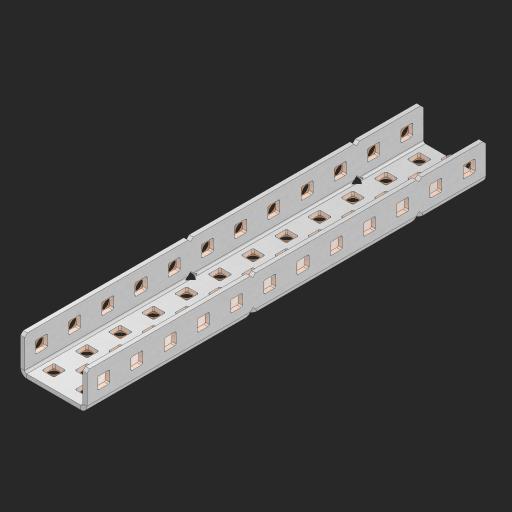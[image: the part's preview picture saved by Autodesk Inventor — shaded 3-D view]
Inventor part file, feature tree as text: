
AUTODESK INVENTOR PART (.ipt)
format: ipt  version: 2023 (Build 270158000, 158)  size: 1,042,944 bytes
history: native  units: in
note: dims shown in document units (in); Inventor stores cm internally (conversion verified against a paired STEP export)
features: other x67, extrude x58, sheet_metal_op x11, sketch x10, pattern_linear x2, mirror x1, chamfer x1
ambient origin geometry x8: Origin, YZ Plane, XZ Plane, XY Plane, X Axis, Y Axis, Z Axis, Center Point
bodies: Solid1 (feature_tree), Body (feature_tree)
feature tree (150):
  sheet_metal_op  "Flanges"
  other  "Flange Pattern Plane"
  other  "Flange Pattern Sketch"
  sheet_metal_op  "Flange Pattern"
  sheet_metal_op  "Body Pattern"
  pattern_linear  "Center Pattern"  Spacing1=0.0625in  [1 undecoded]
  other  "Arc Length"
  mirror  "Notch Mirror"
  pattern_linear  "Notch Pattern"  Spacing1=0.182in  [1 undecoded]
  chamfer  "End Chamfer"
  extrude  "Half Cut"  Depth=0.02in
  sketch  "Sketch1"  dims[d0=1.0in]
  other  "Plate1"
  sketch  "Sketch2"  dims[d1=6.0in]
  other  "Plate2"
  sheet_metal_op  "Bend1"
  sheet_metal_op  "Corner1"
  sketch  "Sketch3"  dims[d2=0.0625in]
  sketch  "Sketch7"  dims[d3=0.0625in]
  other  "Srf1"
  other  "Srf2"
  sketch  "Sketch8"  dims[d4=0.0312in]
  sketch  "Sketch9"  dims[d5=0.125in]
  other  "Srf91"
  sheet_metal_op  "Body Pattern Sketch"
  other  "Srf92"
  sketch  "Sketch13"  dims[d6=0.0625in]
  sketch  "Sketch14"  dims[d7=0.5in d8=90.0deg d9=0.0312in]
  sketch  "Sketch15"  dims[d10=0.25in]
  sketch  "Sketch16"  dims[d11=0.0625in d12=0.0625in d16=0.182in d17=0.02in d18=0.0625in d19=0.0in d20=0.25in d21=0.25in d38=4.7244in d40=0.5in d41=0.7874in d43=1.0in d46=0.172in d47=1.0in d48=0.0in d49=0.182in d50=0.02in d51=0.25in d52=0.25in d53=0.0625in d54=0.0in d55=0.172in d56=1.0in d57=0.0in d58=0.25in d60=4.7244in d62=0.5in d63=0.7874in d65=0.5in d85=0.1473in d86=0.1782in d88=0.04in d89=0.0625in d90=0.0in d91=0.04in d92=0.0491in d95=2.5in d96=0.04in d97=0.25in d98=45.0deg d99=0.25in d100=0.5in d101=0.0in d102=2.497in d106=0.182in d107=0.02in d108=0.5in d109=0.5in d110=0.0625in d111=0.0in d112=0.172in d113=0.5in d114=0.0in d117=0.5in d118=0.5in d119=0.5in]
  other  "Srf786"
  other  "Srf823"
  other  "Srf824"
  other  "Srf825"
  other  "Srf826"
  other  "Srf827"
  other  "Srf828"
  other  "Srf829"
  other  "Srf856"
  other  "Srf857"
  other  "Srf858"
  other  "Srf859"
  other  "Srf860"
  other  "Srf861"
  other  "Srf862"
  other  "Srf889"
  other  "Srf890"
  other  "Srf891"
  other  "Srf892"
  other  "Srf893"
  other  "Srf894"
  other  "Srf895"
  other  "Srf896"
  other  "Srf922"
  other  "Srf923"
  other  "Srf924"
  other  "Srf925"
  other  "Srf926"
  other  "Srf959"
  other  "Srf960"
  other  "Srf961"
  other  "Srf962"
  other  "Srf963"
  other  "Srf996"
  other  "Srf997"
  other  "Srf998"
  other  "Srf1143"
  other  "Srf1144"
  other  "Srf1145"
  other  "Srf1146"
  other  "Srf1147"
  other  "Srf1148"
  other  "Srf1149"
  other  "Srf1150"
  other  "Srf1151"
  other  "Srf1152"
  other  "Srf1199"
  other  "Srf1200"
  other  "Srf1201"
  other  "Srf1202"
  other  "Srf1203"
  other  "Srf1204"
  other  "Srf1205"
  other  "Srf1206"
  other  "Srf1207"
  other  "Srf1208"
  sheet_metal_op  "Flange Stamp"
  sheet_metal_op  "Flange Circle"
  sheet_metal_op  "Body Stamp"
  sheet_metal_op  "Body Circle"
  other  "Center Stamp"
  other  "Center Circle"
  sheet_metal_op  "Notch"
  extrude  "ExtrusionSrf2"  Depth=0.0625in
  extrude  "ExtrusionSrf92"  TaperAngle=0.0deg  [1 undecoded]
  extrude  "ExtrusionSrf823"  Depth=0.5in
  extrude  "ExtrusionSrf824"  Depth=0.5in
  extrude  "ExtrusionSrf825"  Depth=0.5in
  extrude  "ExtrusionSrf826"  Depth=0.5in
  extrude  "ExtrusionSrf827"  Depth=1.0in TaperAngle=0.0deg
  extrude  "ExtrusionSrf828"  Depth=0.5in
  extrude  "ExtrusionSrf829"  Depth=0.02in
  extrude  "ExtrusionSrf856"  Depth=0.5in
  extrude  "ExtrusionSrf857"  Depth=0.5in
  extrude  "ExtrusionSrf858"  Depth=0.0625in
  extrude  "ExtrusionSrf859"  TaperAngle=0.0deg  [1 undecoded]
  extrude  "ExtrusionSrf860"  Depth=0.5in
  extrude  "ExtrusionSrf861"  Depth=1.0in TaperAngle=0.0deg
  extrude  "ExtrusionSrf862"  Depth=0.5in
  extrude  "ExtrusionSrf889"  Depth=0.5in
  extrude  "ExtrusionSrf890"  Depth=0.5in
  extrude  "ExtrusionSrf891"  Depth=0.5in
  extrude  "ExtrusionSrf892"  Depth=0.5in
  extrude  "ExtrusionSrf893"  Depth=0.5in
  extrude  "ExtrusionSrf894"  Depth=0.0625in
  extrude  "ExtrusionSrf895"  TaperAngle=0.0deg  [1 undecoded]
  extrude  "ExtrusionSrf896"  Depth=0.5in
  extrude  "ExtrusionSrf922"  Depth=0.5in
  extrude  "ExtrusionSrf923"  Depth=2.5in
  extrude  "ExtrusionSrf924"  Depth=0.5in TaperAngle=45.0deg
  extrude  "ExtrusionSrf925"  Depth=0.5in
  extrude  "ExtrusionSrf926"  Depth=0.5in TaperAngle=0.0deg
  extrude  "ExtrusionSrf959"  Depth=0.5in
  extrude  "ExtrusionSrf960"  Depth=0.5in
  extrude  "ExtrusionSrf961"  Depth=0.02in
  extrude  "ExtrusionSrf962"  Depth=0.5in
  extrude  "ExtrusionSrf963"  Depth=0.5in
  extrude  "ExtrusionSrf996"  Depth=0.0625in
  extrude  "ExtrusionSrf997"  TaperAngle=0.0deg  [1 undecoded]
  extrude  "ExtrusionSrf998"  Depth=0.5in
  extrude  "ExtrusionSrf1143"  Depth=0.5in TaperAngle=0.0deg
  extrude  "ExtrusionSrf1144"  Depth=0.5in
  extrude  "ExtrusionSrf1145"  Depth=0.5in
  extrude  "ExtrusionSrf1146"  Depth=0.5in
  extrude  "ExtrusionSrf1147"  [1 undecoded]
  extrude  "ExtrusionSrf1148"  [1 undecoded]
  extrude  "ExtrusionSrf1149"  [1 undecoded]
  extrude  "ExtrusionSrf1150"  [1 undecoded]
  extrude  "ExtrusionSrf1151"  [1 undecoded]
  extrude  "ExtrusionSrf1152"  [1 undecoded]
  extrude  "ExtrusionSrf1199"  [1 undecoded]
  extrude  "ExtrusionSrf1200"  [1 undecoded]
  extrude  "ExtrusionSrf1201"  [1 undecoded]
  extrude  "ExtrusionSrf1202"  [1 undecoded]
  extrude  "ExtrusionSrf1203"  [1 undecoded]
  extrude  "ExtrusionSrf1204"  [1 undecoded]
  extrude  "ExtrusionSrf1205"  [1 undecoded]
  extrude  "ExtrusionSrf1206"  [1 undecoded]
  extrude  "ExtrusionSrf1207"  [1 undecoded]
  extrude  "ExtrusionSrf1208"  [1 undecoded]
note: 22 required parameter values undecoded (feature->parameter linkage not recoverable at this tier; creation-order binding heuristic only, values carry confidence <= 0.55)
